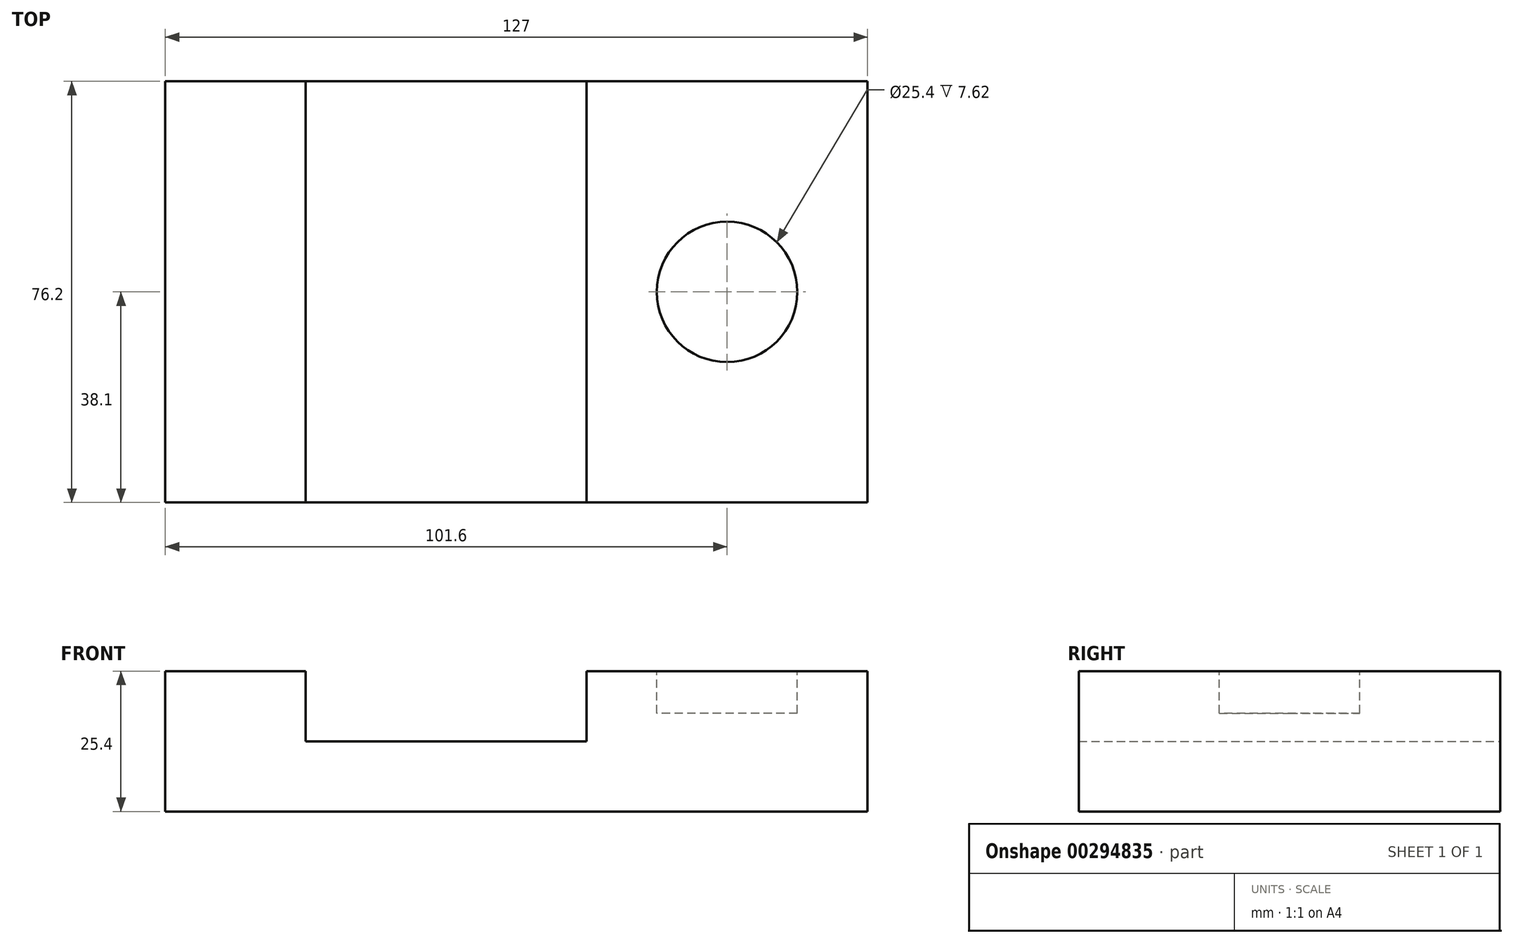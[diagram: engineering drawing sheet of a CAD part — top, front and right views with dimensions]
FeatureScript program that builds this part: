
annotation { "Feature Type Name" : "Feature", "Feature Type Description" : "" }
export const myFeature = defineFeature(function(context is Context, id is Id, definition is map)
    precondition{}
    {
        {
            var Q0;
            Q0=qCreatedBy(makeId("Top.planeOp"),FACE);
            var sketch = newSketch(context, id + "F0", { "sketchPlane" : qUnion([Q0])});
            skLineSegment(sketch, "E0.bottom", {"start": v(0, 0) * mm, "end": v(127, 0) * mm});
            skLineSegment(sketch, "E0.top", {"start": v(0, -76.2) * mm, "end": v(127, -76.2) * mm});
            skLineSegment(sketch, "E0.left", {"start": v(0, 0) * mm, "end": v(0, -76.2) * mm});
            skLineSegment(sketch, "E0.right", {"start": v(127, 0) * mm, "end": v(127, -76.2) * mm});
            skSolve(sketch);
        }
        {
            var Q0;
            Q0 = qSketchRegion(id + "F0", true);
            extrude(context, id + "F1", {"entities" : qUnion([Q0]), "depth" : 25.4 * mm});
        }
        {
            var Q0;
            Q0=makeQuery(id+"F1.opExtrude","CAP_FACE",FACE,{"disambiguationData":[OSD([sQuery(id+"F0.wireOp",EDGE,"E0.bottom"),sQuery(id+"F0.wireOp",EDGE,"E0.top"),sQuery(id+"F0.wireOp",EDGE,"E0.left"),sQuery(id+"F0.wireOp",EDGE,"E0.right")])],"isStart":false});
            var sketch = newSketch(context, id + "F2", { "sketchPlane" : qUnion([Q0])});
            skLineSegment(sketch, "E1.bottom", {"start": v(25.4, -76.2) * mm, "end": v(76.2, -76.2) * mm});
            skLineSegment(sketch, "E1.top", {"start": v(25.4, 0) * mm, "end": v(76.2, 0) * mm});
            skLineSegment(sketch, "E1.left", {"start": v(25.4, -76.2) * mm, "end": v(25.4, 0) * mm});
            skLineSegment(sketch, "E1.right", {"start": v(76.2, -76.2) * mm, "end": v(76.2, 0) * mm});
            skSolve(sketch);
        }
        {
            var Q0;
            Q0=makeQuery(id+"F2.imprint","IMPRINT",FACE,{"disambiguationData":[TD([[makeQuery(id+"F2.imprint","IMPRINT",EDGE,{"derivedFrom":sQuery(id+"F2.wireOp",EDGE,"E1.bottom")}),1.0]])]});
            extrude(context, id + "F3", {"entities" : qUnion([Q0]), "operationType" : NewBodyOperationType.REMOVE, "oppositeDirection" : true, "depth" : 12.7 * mm});
        }
        {
            var Q0;
            {var subQ0=sQuery(id+"F0.wireOp",EDGE,"E0.bottom");var subQ1=sQuery(id+"F0.wireOp",EDGE,"E0.right");var subQ2=sQuery(id+"F0.wireOp",EDGE,"E0.top");Q0=makeQuery(id+"F3.boolean.opBoolean","SPLIT",FACE,{"disambiguationData":[TD([makeQuery(id+"F1.opExtrude","SWEPT_FACE",FACE,{"disambiguationData":[OSD([subQ1])]})])],"derivedFrom":makeQuery(id+"F1.opExtrude","CAP_FACE",FACE,{"disambiguationData":[OSD([subQ0,subQ2,sQuery(id+"F0.wireOp",EDGE,"E0.left"),subQ1])],"isStart":false})});}
            var sketch = newSketch(context, id + "F4", { "sketchPlane" : qUnion([Q0])});
            skCircle(sketch, "E2", {"center": v(101.6, -38.1) * mm, "radius": 12.7 * mm});
            skSolve(sketch);
        }
        {
            var Q0;
            Q0=makeQuery(id+"F4.imprint","IMPRINT",FACE,{"disambiguationData":[TD([[makeQuery(id+"F4.imprint","IMPRINT",EDGE,{"derivedFrom":sQuery(id+"F4.wireOp",EDGE,"E2")}),1.0]])]});
            extrude(context, id + "F5", {"entities" : qUnion([Q0]), "operationType" : NewBodyOperationType.REMOVE, "oppositeDirection" : true, "depth" : 7.62 * mm});
        }
    });
